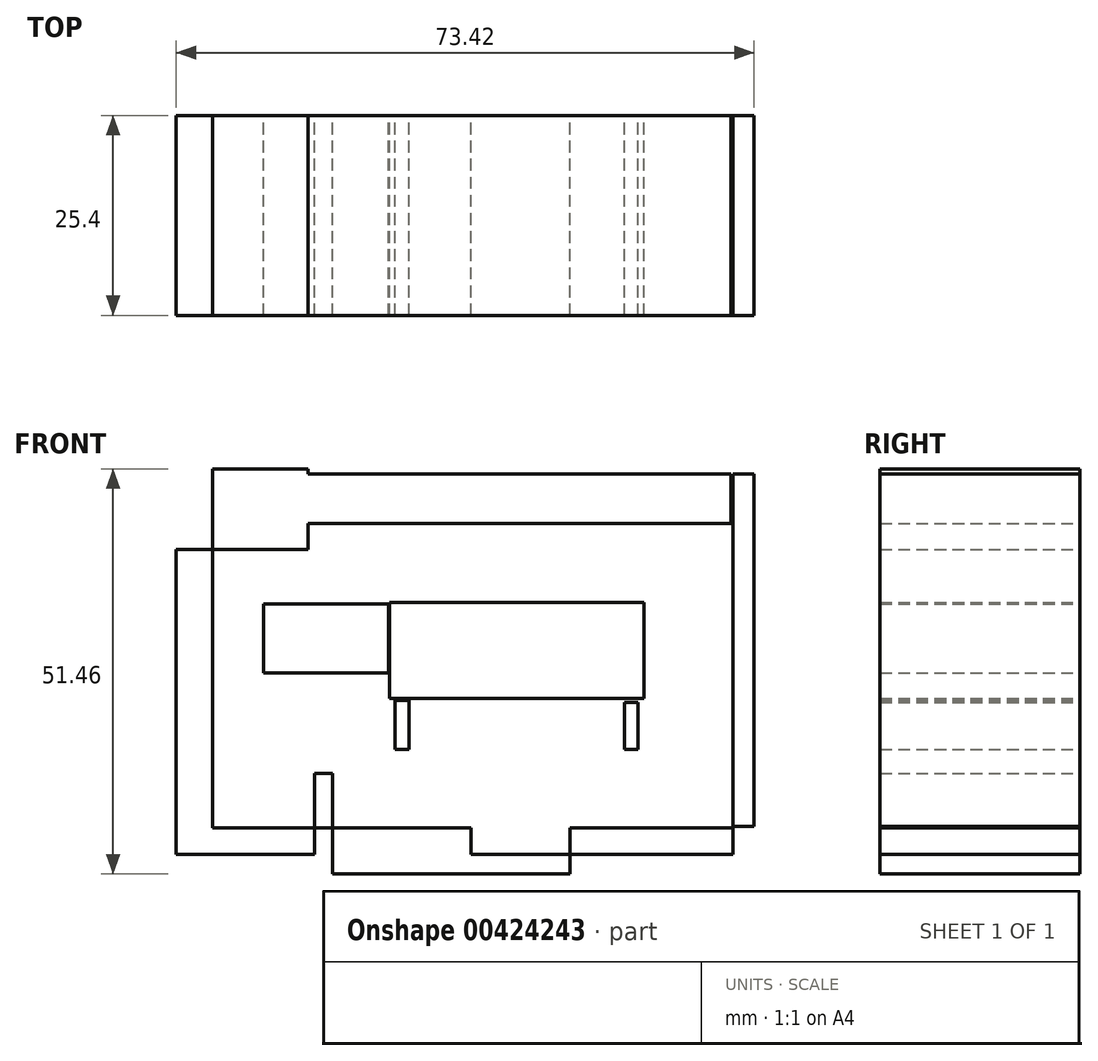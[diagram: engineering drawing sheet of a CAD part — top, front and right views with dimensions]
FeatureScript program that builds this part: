
annotation { "Feature Type Name" : "Feature", "Feature Type Description" : "" }
export const myFeature = defineFeature(function(context is Context, id is Id, definition is map)
    precondition{}
    {
        {
            var Q0;
            Q0=qCreatedBy(makeId("Front.planeOp"),FACE);
            var sketch = newSketch(context, id + "F0", { "sketchPlane" : qUnion([Q0])});
            skLineSegment(sketch, "E0.bottom", {"start": v(18.5, 40.47) * mm, "end": v(50.84, 40.47) * mm});
            skLineSegment(sketch, "E0.top", {"start": v(18.5, 28.28) * mm, "end": v(50.84, 28.28) * mm});
            skLineSegment(sketch, "E0.left", {"start": v(18.5, 40.47) * mm, "end": v(18.5, 28.28) * mm});
            skLineSegment(sketch, "E0.right", {"start": v(50.84, 40.47) * mm, "end": v(50.84, 28.28) * mm});
            skSolve(sketch);
        }
        {
            var Q0;
            Q0=qCreatedBy(makeId("Front.planeOp"),FACE);
            var sketch = newSketch(context, id + "F1", { "sketchPlane" : qUnion([Q0])});
            skLineSegment(sketch, "E1.bottom", {"start": v(19.25, 28.04) * mm, "end": v(20.99, 28.04) * mm});
            skLineSegment(sketch, "E1.top", {"start": v(19.25, 21.82) * mm, "end": v(20.99, 21.82) * mm});
            skLineSegment(sketch, "E1.left", {"start": v(19.25, 28.04) * mm, "end": v(19.25, 21.82) * mm});
            skLineSegment(sketch, "E1.right", {"start": v(20.99, 28.04) * mm, "end": v(20.99, 21.82) * mm});
            skLineSegment(sketch, "E2.bottom", {"start": v(48.35, 27.79) * mm, "end": v(50.1, 27.79) * mm});
            skLineSegment(sketch, "E2.top", {"start": v(48.35, 21.82) * mm, "end": v(50.1, 21.82) * mm});
            skLineSegment(sketch, "E2.left", {"start": v(48.35, 27.79) * mm, "end": v(48.35, 21.82) * mm});
            skLineSegment(sketch, "E2.right", {"start": v(50.1, 27.79) * mm, "end": v(50.1, 21.82) * mm});
            skSolve(sketch);
        }
        {
            var Q0;
            Q0=makeQuery(id+"F0.imprint","IMPRINT",FACE,{"disambiguationData":[TD([[makeQuery(id+"F0.imprint","IMPRINT",EDGE,{"derivedFrom":sQuery(id+"F0.wireOp",EDGE,"E0.bottom")}),-1.0]])]});
            extrude(context, id + "F2", {"entities" : qUnion([Q0]), "depth" : 25.4 * mm});
        }
        {
            var Q0;
            Q0 = qSketchRegion(id + "F1", true);
            var Q1;
            Q1 = qSketchRegion(id + "FK28Iea4482pQiV_0", true);
            extrude(context, id + "F3", {"entities" : qUnion([Q0, Q1]), "depth" : 25.4 * mm});
        }
        {
            var Q0;
            Q0=qCreatedBy(makeId("Front.planeOp"),FACE);
            var sketch = newSketch(context, id + "F4", { "sketchPlane" : qUnion([Q0])});
            skLineSegment(sketch, "E3.bottom", {"start": v(18.4, 40.27) * mm, "end": v(2.51, 40.27) * mm});
            skLineSegment(sketch, "E3.top", {"start": v(18.4, 31.48) * mm, "end": v(2.51, 31.48) * mm});
            skLineSegment(sketch, "E3.left", {"start": v(18.4, 40.27) * mm, "end": v(18.4, 31.48) * mm});
            skLineSegment(sketch, "E3.right", {"start": v(2.51, 40.27) * mm, "end": v(2.51, 31.48) * mm});
            skLineSegment(sketch, "E4.bottom", {"start": v(9, 20.4) * mm, "end": v(9, 20.4) * mm});
            skLineSegment(sketch, "E4.top", {"start": v(9, 18.72) * mm, "end": v(9, 18.72) * mm});
            skLineSegment(sketch, "E4.left", {"start": v(9, 20.4) * mm, "end": v(9, 18.72) * mm});
            skLineSegment(sketch, "E4.right", {"start": v(9, 20.4) * mm, "end": v(9, 18.72) * mm});
            skLineSegment(sketch, "E5.bottom", {"start": v(9, 18.72) * mm, "end": v(11.3, 18.72) * mm});
            skLineSegment(sketch, "E5.top", {"start": v(9, 11.82) * mm, "end": v(11.3, 11.82) * mm});
            skLineSegment(sketch, "E5.left", {"start": v(9, 18.72) * mm, "end": v(9, 11.82) * mm});
            skLineSegment(sketch, "E5.right", {"start": v(11.3, 18.72) * mm, "end": v(11.3, 11.82) * mm});
            skLineSegment(sketch, "E6.bottom", {"start": v(11.3, 11.82) * mm, "end": v(28.87, 11.82) * mm});
            skLineSegment(sketch, "E6.top", {"start": v(11.3, 5.96) * mm, "end": v(28.87, 5.96) * mm});
            skLineSegment(sketch, "E6.left", {"start": v(11.3, 11.82) * mm, "end": v(11.3, 5.96) * mm});
            skLineSegment(sketch, "E6.right", {"start": v(28.87, 11.82) * mm, "end": v(28.87, 5.96) * mm});
            skLineSegment(sketch, "E7.bottom", {"start": v(28.87, 5.96) * mm, "end": v(41.42, 5.96) * mm});
            skLineSegment(sketch, "E7.top", {"start": v(28.87, 8.47) * mm, "end": v(41.42, 8.47) * mm});
            skLineSegment(sketch, "E7.left", {"start": v(28.87, 5.96) * mm, "end": v(28.87, 8.47) * mm});
            skLineSegment(sketch, "E7.right", {"start": v(41.42, 5.96) * mm, "end": v(41.42, 8.47) * mm});
            skLineSegment(sketch, "E8.bottom", {"start": v(41.42, 8.47) * mm, "end": v(62.13, 8.47) * mm});
            skLineSegment(sketch, "E8.top", {"start": v(41.42, 11.82) * mm, "end": v(62.13, 11.82) * mm});
            skLineSegment(sketch, "E8.left", {"start": v(41.42, 8.47) * mm, "end": v(41.42, 11.82) * mm});
            skLineSegment(sketch, "E8.right", {"start": v(62.13, 8.47) * mm, "end": v(62.13, 11.82) * mm});
            skLineSegment(sketch, "E9.bottom", {"start": v(62.13, 12.03) * mm, "end": v(64.84, 12.03) * mm});
            skLineSegment(sketch, "E9.top", {"start": v(62.13, 29.18) * mm, "end": v(64.84, 29.18) * mm});
            skLineSegment(sketch, "E9.left", {"start": v(62.13, 12.03) * mm, "end": v(62.13, 29.18) * mm});
            skLineSegment(sketch, "E9.right", {"start": v(64.84, 12.03) * mm, "end": v(64.84, 29.18) * mm});
            skLineSegment(sketch, "E10.bottom", {"start": v(64.84, 29.18) * mm, "end": v(62.13, 29.18) * mm});
            skLineSegment(sketch, "E10.top", {"start": v(64.84, 56.8) * mm, "end": v(62.13, 56.8) * mm});
            skLineSegment(sketch, "E10.left", {"start": v(64.84, 29.18) * mm, "end": v(64.84, 56.8) * mm});
            skLineSegment(sketch, "E10.right", {"start": v(62.13, 29.18) * mm, "end": v(62.13, 56.8) * mm});
            skLineSegment(sketch, "E11.bottom", {"start": v(61.92, 56.8) * mm, "end": v(41.42, 56.8) * mm});
            skLineSegment(sketch, "E11.top", {"start": v(61.92, 50.52) * mm, "end": v(41.42, 50.52) * mm});
            skLineSegment(sketch, "E11.left", {"start": v(61.92, 56.8) * mm, "end": v(61.92, 50.52) * mm});
            skLineSegment(sketch, "E11.right", {"start": v(41.42, 56.8) * mm, "end": v(41.42, 50.52) * mm});
            skLineSegment(sketch, "E12.bottom", {"start": v(42.67, 50.52) * mm, "end": v(8.16, 50.52) * mm});
            skLineSegment(sketch, "E12.top", {"start": v(42.67, 56.8) * mm, "end": v(8.16, 56.8) * mm});
            skLineSegment(sketch, "E12.left", {"start": v(42.67, 50.52) * mm, "end": v(42.67, 56.8) * mm});
            skLineSegment(sketch, "E12.right", {"start": v(8.16, 50.52) * mm, "end": v(8.16, 56.8) * mm});
            skLineSegment(sketch, "E13.bottom", {"start": v(8.16, 57.42) * mm, "end": v(-3.97, 57.42) * mm});
            skLineSegment(sketch, "E13.top", {"start": v(8.16, 47.17) * mm, "end": v(-3.97, 47.17) * mm});
            skLineSegment(sketch, "E13.left", {"start": v(8.16, 57.42) * mm, "end": v(8.16, 47.17) * mm});
            skLineSegment(sketch, "E13.right", {"start": v(-3.97, 57.42) * mm, "end": v(-3.97, 47.17) * mm});
            skLineSegment(sketch, "E14.bottom", {"start": v(-3.97, 47.17) * mm, "end": v(-8.58, 47.17) * mm});
            skLineSegment(sketch, "E14.top", {"start": v(-3.97, 11.82) * mm, "end": v(-8.58, 11.82) * mm});
            skLineSegment(sketch, "E14.left", {"start": v(-3.97, 47.17) * mm, "end": v(-3.97, 11.82) * mm});
            skLineSegment(sketch, "E14.right", {"start": v(-8.58, 47.17) * mm, "end": v(-8.58, 11.82) * mm});
            skLineSegment(sketch, "E15.bottom", {"start": v(-8.58, 11.82) * mm, "end": v(9, 11.82) * mm});
            skLineSegment(sketch, "E15.top", {"start": v(-8.58, 8.47) * mm, "end": v(9, 8.47) * mm});
            skLineSegment(sketch, "E15.left", {"start": v(-8.58, 11.82) * mm, "end": v(-8.58, 8.47) * mm});
            skLineSegment(sketch, "E15.right", {"start": v(9, 11.82) * mm, "end": v(9, 8.47) * mm});
            skSolve(sketch);
        }
        {
            var Q0;
            Q0 = qSketchRegion(id + "F4", true);
            extrude(context, id + "F5", {"entities" : qUnion([Q0]), "depth" : 25.4 * mm});
        }
    });
